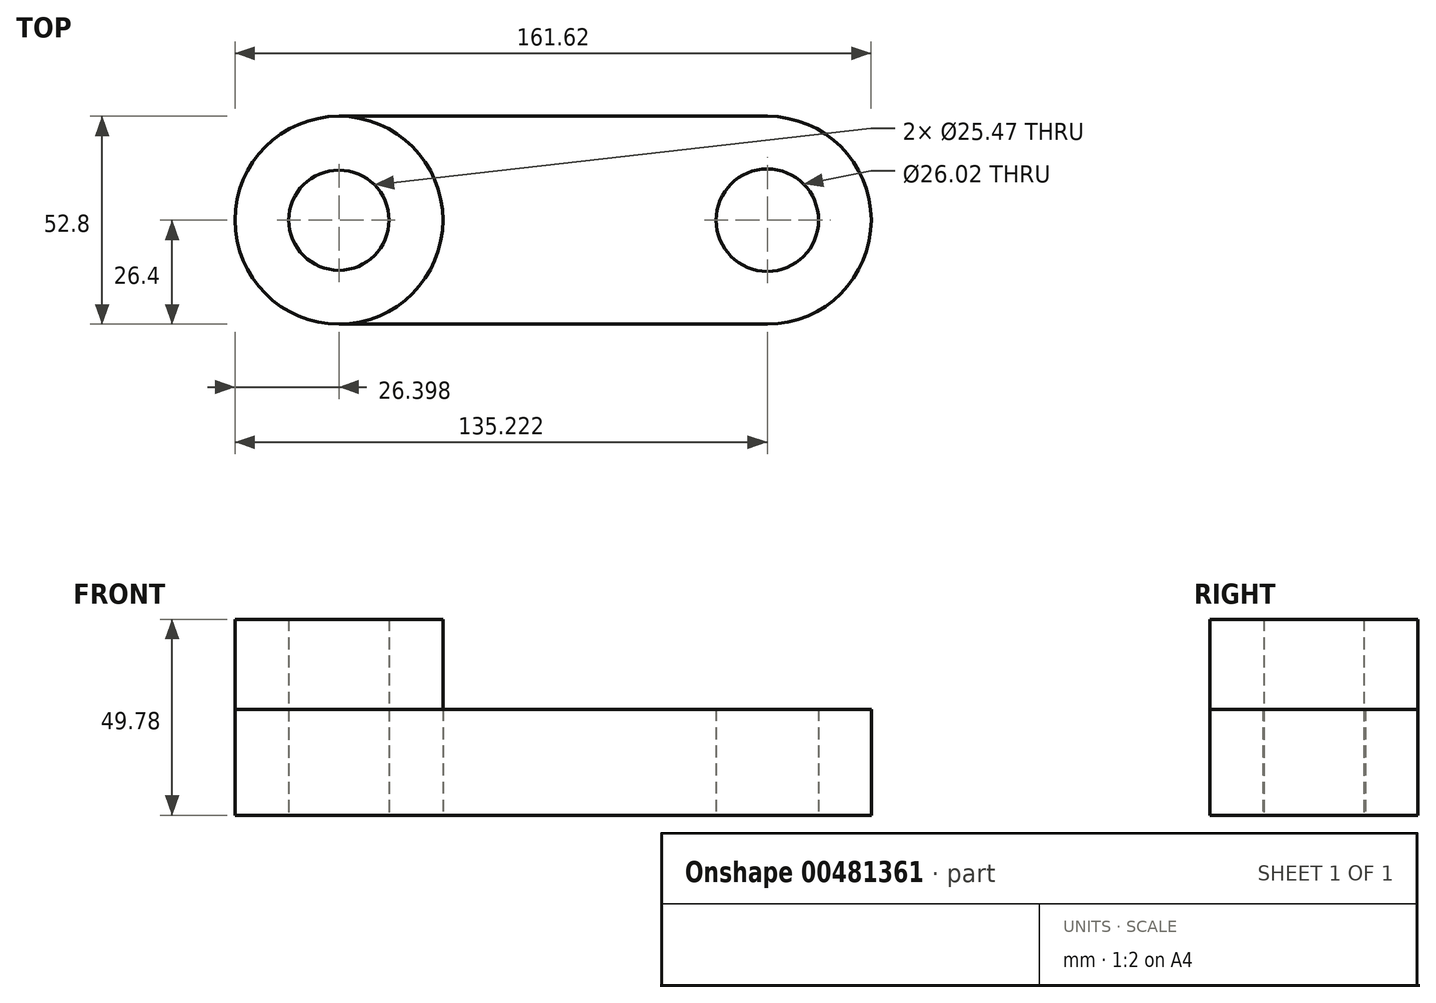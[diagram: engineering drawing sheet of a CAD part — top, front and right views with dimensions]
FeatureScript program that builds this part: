
annotation { "Feature Type Name" : "Feature", "Feature Type Description" : "" }
export const myFeature = defineFeature(function(context is Context, id is Id, definition is map)
    precondition{}
    {
        {
            var Q0;
            Q0=qCreatedBy(makeId("Top.planeOp"),FACE);
            var sketch = newSketch(context, id + "F0", { "sketchPlane" : qUnion([Q0])});
            skLineSegment(sketch, "E0.bottom", {"start": v(54.41, -26.4) * mm, "end": v(-54.41, -26.4) * mm});
            skLineSegment(sketch, "E0.top", {"start": v(54.41, 26.4) * mm, "end": v(-54.41, 26.4) * mm});
            skPoint(sketch, "E0.middle", {"position": v(0, 0) * mm});
            skCircle(sketch, "E1", {"center": v(-54.41, 0) * mm, "radius": 26.4 * mm});
            skCircle(sketch, "E2", {"center": v(-54.41, 0) * mm, "radius": 12.73 * mm});
            skArc(sketch, "E3", {"start": v(54.41, -26.4) * mm, "mid": v(80.81, 0) * mm, "end": v(54.41, 26.4) * mm});
            skCircle(sketch, "E4", {"center": v(54.41, 0) * mm, "radius": 13.01 * mm});
            skSolve(sketch);
        }
        {
            var Q0;
            Q0=makeQuery(id+"F0.imprint","IMPRINT",FACE,{"disambiguationData":[TD([[makeQuery(id+"F0.imprint","IMPRINT",EDGE,{"derivedFrom":sQuery(id+"F0.wireOp",EDGE,"E2")}),-1.0]])]});
            extrude(context, id + "F1", {"entities" : qUnion([Q0]), "depth" : 49.78 * mm});
        }
        {
            var Q0;
            Q0 = qSketchRegion(id + "F0", true);
            extrude(context, id + "F2", {"entities" : qUnion([Q0]), "depth" : 26.92 * mm});
        }
    });
